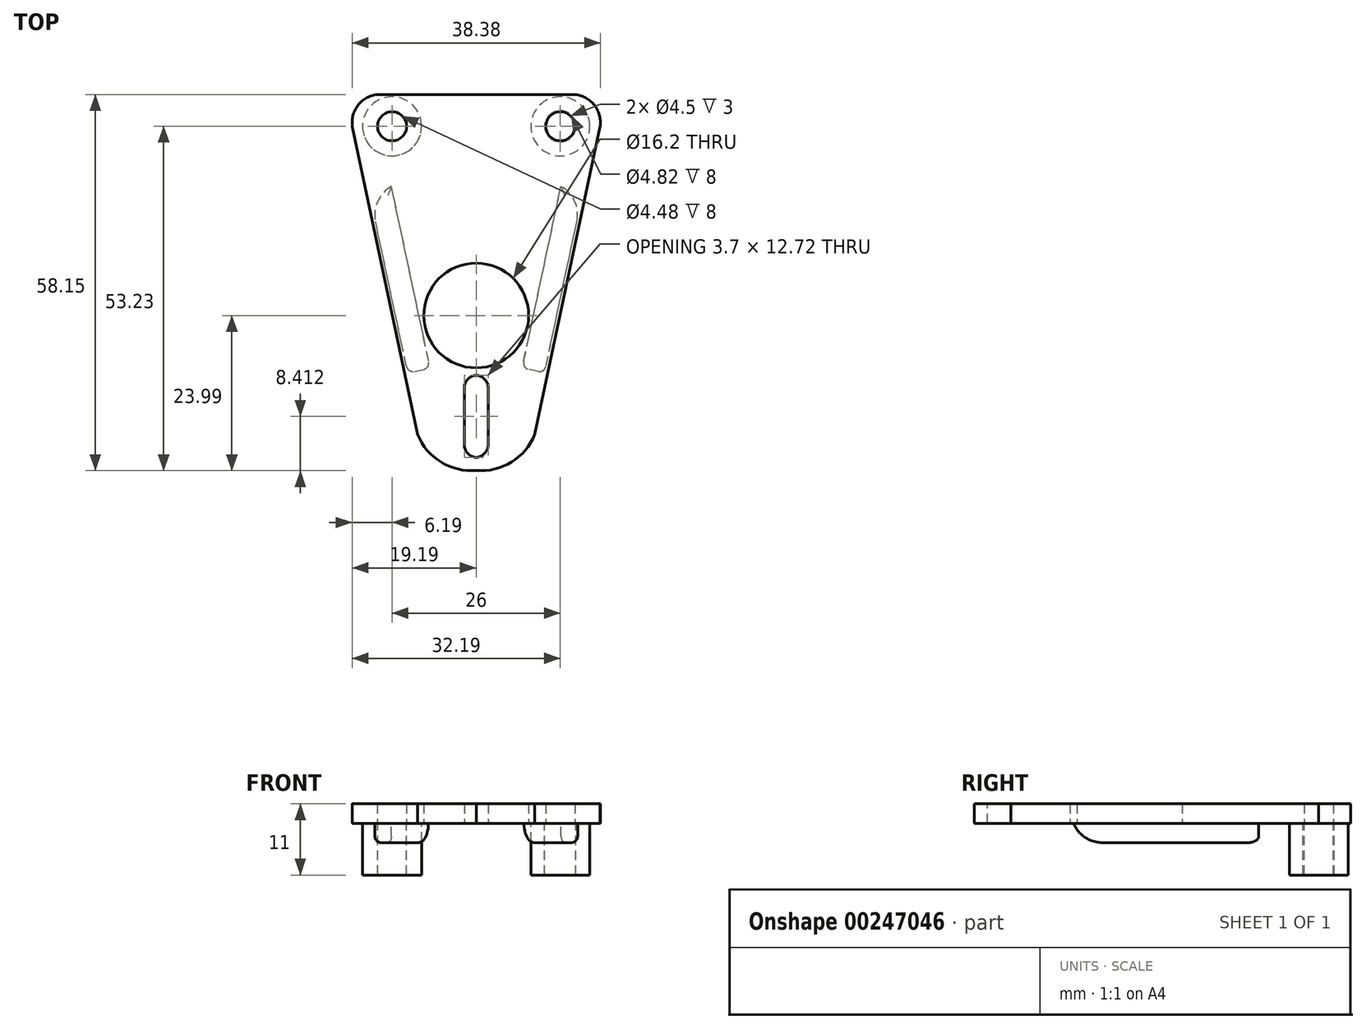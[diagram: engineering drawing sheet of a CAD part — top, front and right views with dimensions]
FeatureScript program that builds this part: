
annotation { "Feature Type Name" : "Feature", "Feature Type Description" : "" }
export const myFeature = defineFeature(function(context is Context, id is Id, definition is map)
    precondition{}
    {
        {
            var Q0;
            Q0=qCreatedBy(makeId("Top.planeOp"),FACE);
            var sketch = newSketch(context, id + "F0", { "sketchPlane" : qUnion([Q0])});
            skCircle(sketch, "E0", {"center": v(0, 0) * mm, "radius": 6.15 * mm, "construction": true});
            skCircle(sketch, "E1", {"center": v(0, 0) * mm, "radius": 25.5 * mm, "construction": true});
            skCircle(sketch, "E2", {"center": v(13, 29.24) * mm, "radius": 2.25 * mm});
            skCircle(sketch, "E3", {"center": v(-13, 29.24) * mm, "radius": 2.25 * mm});
            skLineSegment(sketch, "E4", {"start": v(0, 34.16) * mm, "end": v(14.84, 34.16) * mm});
            skArc(sketch, "E5", {"start": v(19.14, 29.2) * mm, "mid": v(18.13, 32.66) * mm, "end": v(14.84, 34.16) * mm});
            skArc(sketch, "E6", {"start": v(0, -23.96) * mm, "mid": v(5.45, -22.66) * mm, "end": v(9.07, -18.37) * mm});
            skLineSegment(sketch, "E7", {"start": v(9.07, -18.37) * mm, "end": v(19.14, 29.2) * mm});
            skArc(sketch, "E8.MirrorCS", {"start": v(0, -23.96) * mm, "mid": v(-5.45, -22.66) * mm, "end": v(-9.07, -18.37) * mm});
            skLineSegment(sketch, "E9.MirrorCS", {"start": v(0, 34.16) * mm, "end": v(-14.84, 34.16) * mm});
            skLineSegment(sketch, "E10.MirrorCS", {"start": v(-9.07, -18.37) * mm, "end": v(-19.14, 29.2) * mm});
            skArc(sketch, "E11.MirrorCS", {"start": v(-19.14, 29.2) * mm, "mid": v(-18.13, 32.66) * mm, "end": v(-14.84, 34.16) * mm});
            skCircle(sketch, "E12", {"center": v(0, 0) * mm, "radius": 8.1 * mm});
            skLineSegment(sketch, "E13.bottom", {"start": v(-1.85, -9.21) * mm, "end": v(1.85, -9.21) * mm});
            skLineSegment(sketch, "E13.top", {"start": v(-1.85, -21.94) * mm, "end": v(1.85, -21.94) * mm});
            skLineSegment(sketch, "E13.left", {"start": v(-1.85, -9.21) * mm, "end": v(-1.85, -21.94) * mm});
            skLineSegment(sketch, "E13.right", {"start": v(1.85, -9.21) * mm, "end": v(1.85, -21.94) * mm});
            skSolve(sketch);
        }
        {
            var Q0;
            Q0 = qSketchRegion(id + "F0", true);
            extrude(context, id + "F1", {"entities" : qUnion([Q0]), "depth" : 3 * mm});
        }
        {
            var Q0;
            Q0=makeQuery(id+"F1.opExtrude","SWEPT_EDGE",EDGE,{"disambiguationData":[OSD([sQuery(id+"F0.wireOp",EDGE,"E13.bottom"),sQuery(id+"F0.wireOp",EDGE,"E13.left")])]});
            var Q1;
            Q1=makeQuery(id+"F1.opExtrude","SWEPT_EDGE",EDGE,{"disambiguationData":[OSD([sQuery(id+"F0.wireOp",EDGE,"E13.bottom"),sQuery(id+"F0.wireOp",EDGE,"E13.right")])]});
            var Q2;
            Q2=makeQuery(id+"F1.opExtrude","SWEPT_EDGE",EDGE,{"disambiguationData":[OSD([sQuery(id+"F0.wireOp",EDGE,"E13.top"),sQuery(id+"F0.wireOp",EDGE,"E13.left")])]});
            var Q3;
            Q3=makeQuery(id+"F1.opExtrude","SWEPT_EDGE",EDGE,{"disambiguationData":[OSD([sQuery(id+"F0.wireOp",EDGE,"E13.top"),sQuery(id+"F0.wireOp",EDGE,"E13.right")])]});
            fillet(context, id + "F2", {"entities" : qUnion([Q0, Q1, Q2, Q3]), "radius" : 2 * mm, "tangentPropagation" : true, "allowEdgeOverflow" : false});
        }
        {
            var Q0;
            Q0=makeQuery(id+"F1.opExtrude","CAP_FACE",FACE,{"disambiguationData":[OSD([sQuery(id+"F0.wireOp",EDGE,"E2"),sQuery(id+"F0.wireOp",EDGE,"E3"),sQuery(id+"F0.wireOp",EDGE,"E4"),sQuery(id+"F0.wireOp",EDGE,"E5"),sQuery(id+"F0.wireOp",EDGE,"E6"),sQuery(id+"F0.wireOp",EDGE,"E7"),sQuery(id+"F0.wireOp",EDGE,"E8.MirrorCS"),sQuery(id+"F0.wireOp",EDGE,"E9.MirrorCS"),sQuery(id+"F0.wireOp",EDGE,"E10.MirrorCS"),sQuery(id+"F0.wireOp",EDGE,"E11.MirrorCS"),sQuery(id+"F0.wireOp",EDGE,"E12"),sQuery(id+"F0.wireOp",EDGE,"E13.bottom"),sQuery(id+"F0.wireOp",EDGE,"E13.top"),sQuery(id+"F0.wireOp",EDGE,"E13.left"),sQuery(id+"F0.wireOp",EDGE,"E13.right")])],"isStart":true});
            var sketch = newSketch(context, id + "F3", { "sketchPlane" : qUnion([Q0])});
            skCircle(sketch, "E14", {"center": v(13, -29.24) * mm, "radius": 4.56 * mm});
            skCircle(sketch, "E15", {"center": v(-13, -29.24) * mm, "radius": 4.56 * mm});
            skCircle(sketch, "E16", {"center": v(13, -29.24) * mm, "radius": 2.41 * mm});
            skCircle(sketch, "E17", {"center": v(-13, -29.24) * mm, "radius": 2.24 * mm});
            skSolve(sketch);
        }
        {
            var Q0;
            Q0 = qSketchRegion(id + "F3", true);
            extrude(context, id + "F4", {"entities" : qUnion([Q0]), "operationType" : NewBodyOperationType.ADD, "depth" : 8 * mm});
        }
        {
            var Q0;
            {var subQ10=sQuery(id+"F0.wireOp",EDGE,"E13.right");var subQ11=sQuery(id+"F0.wireOp",EDGE,"E13.top");var subQ12=sQuery(id+"F0.wireOp",EDGE,"E11.MirrorCS");var subQ13=sQuery(id+"F0.wireOp",EDGE,"E13.bottom");var subQ14=sQuery(id+"F0.wireOp",EDGE,"E8.MirrorCS");var subQ15=sQuery(id+"F0.wireOp",EDGE,"E7");var subQ16=sQuery(id+"F0.wireOp",EDGE,"E13.left");var subQ17=sQuery(id+"F0.wireOp",EDGE,"E10.MirrorCS");var subQ18=sQuery(id+"F0.wireOp",EDGE,"E6");var subQ19=sQuery(id+"F0.wireOp",EDGE,"E5");var subQ20=sQuery(id+"F0.wireOp",EDGE,"E9.MirrorCS");var subQ21=sQuery(id+"F0.wireOp",EDGE,"E4");var subQ22=sQuery(id+"F0.wireOp",EDGE,"E12");Q0=makeQuery(id+"F4.boolean.opBoolean","SPLIT",FACE,{"disambiguationData":[TD([makeQuery(id+"F1.opExtrude","SWEPT_FACE",FACE,{"disambiguationData":[OSD([subQ19])]})])],"derivedFrom":makeQuery(id+"F1.opExtrude","CAP_FACE",FACE,{"disambiguationData":[OSD([sQuery(id+"F0.wireOp",EDGE,"E2"),sQuery(id+"F0.wireOp",EDGE,"E3"),subQ21,subQ19,subQ18,subQ15,subQ14,subQ20,subQ17,subQ12,subQ22,subQ13,subQ11,subQ16,subQ10])],"isStart":true})});}
            var sketch = newSketch(context, id + "F5", { "sketchPlane" : qUnion([Q0])});
            skLineSegment(sketch, "E18.bottom", {"start": v(-10.58, 8.87) * mm, "end": v(-7.12, 8.13) * mm});
            skLineSegment(sketch, "E18.top", {"start": v(-16.56, -19.22) * mm, "end": v(-13.1, -19.95) * mm});
            skLineSegment(sketch, "E18.left", {"start": v(-10.58, 8.87) * mm, "end": v(-16.56, -19.22) * mm});
            skLineSegment(sketch, "E18.right", {"start": v(-7.12, 8.13) * mm, "end": v(-13.1, -19.95) * mm});
            skLineSegment(sketch, "E19.MirrorCS", {"start": v(10.58, 8.87) * mm, "end": v(7.12, 8.13) * mm});
            skLineSegment(sketch, "E20.MirrorCS", {"start": v(7.12, 8.13) * mm, "end": v(13.1, -19.95) * mm});
            skLineSegment(sketch, "E21.MirrorCS", {"start": v(16.56, -19.22) * mm, "end": v(13.1, -19.95) * mm});
            skLineSegment(sketch, "E22.MirrorCS", {"start": v(10.58, 8.87) * mm, "end": v(16.56, -19.22) * mm});
            skSolve(sketch);
        }
        {
            var Q0;
            Q0 = qSketchRegion(id + "F5", true);
            extrude(context, id + "F6", {"entities" : qUnion([Q0]), "operationType" : NewBodyOperationType.ADD, "depth" : 3 * mm});
        }
        {
            var Q0;
            Q0=makeQuery(id+"F6.opExtrude","SWEPT_EDGE",EDGE,{"disambiguationData":[OSD([sQuery(id+"F5.wireOp",EDGE,"E18.top"),sQuery(id+"F5.wireOp",EDGE,"E18.left")])]});
            var Q1;
            Q1=makeQuery(id+"F6.opExtrude","SWEPT_EDGE",EDGE,{"disambiguationData":[OSD([sQuery(id+"F5.wireOp",EDGE,"E21.MirrorCS"),sQuery(id+"F5.wireOp",EDGE,"E22.MirrorCS")])]});
            var Q2;
            Q2=makeQuery(id+"F6.opExtrude","CAP_EDGE",EDGE,{"disambiguationData":[OSD([sQuery(id+"F5.wireOp",EDGE,"E19.MirrorCS")])],"isStart":false});
            var Q3;
            Q3=makeQuery(id+"F6.opExtrude","CAP_EDGE",EDGE,{"disambiguationData":[OSD([sQuery(id+"F5.wireOp",EDGE,"E18.bottom")])],"isStart":false});
            fillet(context, id + "F7", {"entities" : qUnion([Q0, Q1, Q2, Q3]), "radius" : 5 * mm, "tangentPropagation" : true, "allowEdgeOverflow" : false});
        }
        {
            var Q0;
            Q0=makeQuery(id+"F6.opExtrude","CAP_EDGE",EDGE,{"disambiguationData":[OSD([sQuery(id+"F5.wireOp",EDGE,"E18.right")])],"isStart":false});
            var Q1;
            Q1=makeQuery(id+"F6.opExtrude","CAP_EDGE",EDGE,{"disambiguationData":[OSD([sQuery(id+"F5.wireOp",EDGE,"E20.MirrorCS")])],"isStart":false});
            var Q2;
            Q2=makeQuery(id+"F6.opExtrude","CAP_EDGE",EDGE,{"disambiguationData":[OSD([sQuery(id+"F5.wireOp",EDGE,"E22.MirrorCS")])],"isStart":false});
            var Q3;
            Q3=makeQuery(id+"F6.opExtrude","CAP_EDGE",EDGE,{"disambiguationData":[OSD([sQuery(id+"F5.wireOp",EDGE,"E18.left")])],"isStart":false});
            fillet(context, id + "F8", {"entities" : qUnion([Q0, Q1, Q2, Q3]), "radius" : 1 * mm, "tangentPropagation" : true, "allowEdgeOverflow" : false});
        }
    });
